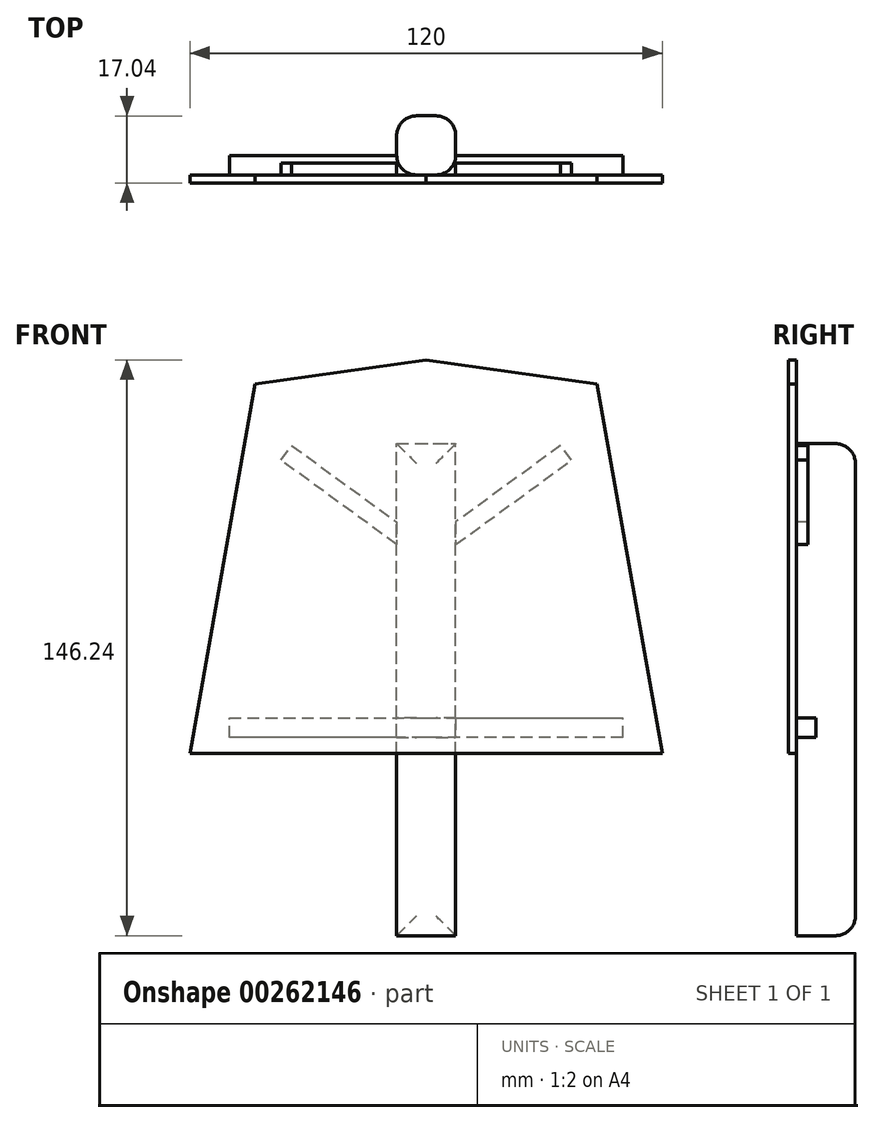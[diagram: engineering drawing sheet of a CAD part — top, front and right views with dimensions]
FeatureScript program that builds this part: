
annotation { "Feature Type Name" : "Feature", "Feature Type Description" : "" }
export const myFeature = defineFeature(function(context is Context, id is Id, definition is map)
    precondition{}
    {
        {
            var Q0;
            Q0=qCreatedBy(makeId("Top.planeOp"),FACE);
            var sketch = newSketch(context, id + "F0", { "sketchPlane" : qUnion([Q0])});
            skLineSegment(sketch, "E0.bottom", {"start": v(-7.5, 15.04) * mm, "end": v(7.5, 15.04) * mm});
            skLineSegment(sketch, "E0.top", {"start": v(-7.5, 0.04) * mm, "end": v(7.5, 0.04) * mm});
            skLineSegment(sketch, "E0.left", {"start": v(-7.5, 15.04) * mm, "end": v(-7.5, 0.04) * mm});
            skLineSegment(sketch, "E0.right", {"start": v(7.5, 15.04) * mm, "end": v(7.5, 0.04) * mm});
            skSolve(sketch);
        }
        {
            var Q0;
            Q0 = qSketchRegion(id + "F0", true);
            extrude(context, id + "F1", {"entities" : qUnion([Q0]), "oppositeDirection" : true, "depth" : 25 * mm});
        }
        {
            var Q0;
            Q0=makeQuery(id+"F1.opExtrude","CAP_FACE",FACE,{"disambiguationData":[OSD([sQuery(id+"F0.wireOp",EDGE,"E0.bottom"),sQuery(id+"F0.wireOp",EDGE,"E0.top"),sQuery(id+"F0.wireOp",EDGE,"E0.left"),sQuery(id+"F0.wireOp",EDGE,"E0.right")])],"isStart":true});
            extrude(context, id + "F2", {"entities" : qUnion([Q0]), "operationType" : NewBodyOperationType.ADD, "depth" : 100 * mm});
        }
        {
            var Q0;
            Q0=qCreatedBy(makeId("Front.planeOp"),FACE);
            var sketch = newSketch(context, id + "F3", { "sketchPlane" : qUnion([Q0])});
            skLineSegment(sketch, "E1", {"start": v(60, 21.24) * mm, "end": v(43.44, 115.13) * mm});
            skLineSegment(sketch, "E2", {"start": v(0, 121.24) * mm, "end": v(43.44, 115.13) * mm});
            skLineSegment(sketch, "E3", {"start": v(0, 21.24) * mm, "end": v(60, 21.24) * mm});
            skLineSegment(sketch, "E4", {"start": v(0, 21.24) * mm, "end": v(0, 121.24) * mm});
            skLineSegment(sketch, "E5.MirrorCS", {"start": v(0, 121.24) * mm, "end": v(-43.44, 115.13) * mm});
            skLineSegment(sketch, "E6.MirrorCS", {"start": v(-60, 21.24) * mm, "end": v(-43.44, 115.13) * mm});
            skLineSegment(sketch, "E7.MirrorCS", {"start": v(0, 21.24) * mm, "end": v(-60, 21.24) * mm});
            skSolve(sketch);
        }
        {
            var Q0;
            Q0=makeQuery(id+"F3.imprint","IMPRINT",FACE,{"disambiguationData":[TD([[makeQuery(id+"F3.imprint","IMPRINT",EDGE,{"derivedFrom":sQuery(id+"F3.wireOp",EDGE,"E4")}),1.0]])]});
            var Q1;
            Q1=makeQuery(id+"F3.imprint","IMPRINT",FACE,{"disambiguationData":[TD([[makeQuery(id+"F3.imprint","IMPRINT",EDGE,{"derivedFrom":sQuery(id+"F3.wireOp",EDGE,"E1")}),1.0]])]});
            extrude(context, id + "F4", {"entities" : qUnion([Q0, Q1]), "operationType" : NewBodyOperationType.ADD, "depth" : 2 * mm});
        }
        {
            var Q0;
            Q0=qCreatedBy(makeId("Front.planeOp"),FACE);
            var sketch = newSketch(context, id + "F5", { "sketchPlane" : qUnion([Q0])});
            skLineSegment(sketch, "E8", {"start": v(0, 25.31) * mm, "end": v(-50, 25.31) * mm});
            skLineSegment(sketch, "E9", {"start": v(-50, 25.31) * mm, "end": v(-50, 30.31) * mm});
            skLineSegment(sketch, "E10", {"start": v(-50, 30.31) * mm, "end": v(0, 30.31) * mm});
            skLineSegment(sketch, "E11", {"start": v(0, 30.31) * mm, "end": v(0, 25.31) * mm});
            skLineSegment(sketch, "E12.MirrorCS", {"start": v(50, 30.31) * mm, "end": v(0, 30.31) * mm});
            skLineSegment(sketch, "E13.MirrorCS", {"start": v(0, 25.31) * mm, "end": v(50, 25.31) * mm});
            skLineSegment(sketch, "E14.MirrorCS", {"start": v(50, 25.31) * mm, "end": v(50, 30.31) * mm});
            skSolve(sketch);
        }
        {
            var Q0;
            Q0=makeQuery(id+"F5.imprint","IMPRINT",FACE,{"disambiguationData":[TD([[makeQuery(id+"F5.imprint","IMPRINT",EDGE,{"derivedFrom":sQuery(id+"F5.wireOp",EDGE,"E8")}),-1.0]])]});
            var Q1;
            Q1=makeQuery(id+"F5.imprint","IMPRINT",FACE,{"disambiguationData":[TD([[makeQuery(id+"F5.imprint","IMPRINT",EDGE,{"derivedFrom":sQuery(id+"F5.wireOp",EDGE,"E11")}),1.0]])]});
            extrude(context, id + "F6", {"entities" : qUnion([Q0, Q1]), "oppositeDirection" : true, "depth" : 5 * mm});
        }
        {
            var Q0;
            Q0=makeQuery(id+"F1.opExtrude","SWEPT_BODY",BODY,{"disambiguationData":[OSD([sQuery(id+"F0.wireOp",EDGE,"E0.bottom"),sQuery(id+"F0.wireOp",EDGE,"E0.top"),sQuery(id+"F0.wireOp",EDGE,"E0.left"),sQuery(id+"F0.wireOp",EDGE,"E0.right")])]});
            var Q1;
            Q1=makeQuery(id+"F6.opExtrude","SWEPT_BODY",BODY,{"disambiguationData":[OSD([sQuery(id+"F5.wireOp",EDGE,"E8"),sQuery(id+"F5.wireOp",EDGE,"E9"),sQuery(id+"F5.wireOp",EDGE,"E10"),sQuery(id+"F5.wireOp",EDGE,"E12.MirrorCS"),sQuery(id+"F5.wireOp",EDGE,"E13.MirrorCS"),sQuery(id+"F5.wireOp",EDGE,"E14.MirrorCS")])]});
            booleanBodies(context, id + "F7", {"operationType" : BooleanOperationType.UNION, "tools" : qUnion([Q0, Q1])});
        }
        {
            var Q0;
            Q0=makeQuery(id+"F4.opExtrude","CAP_FACE",FACE,{"disambiguationData":[OSD([sQuery(id+"F3.wireOp",EDGE,"E1"),sQuery(id+"F3.wireOp",EDGE,"E2"),sQuery(id+"F3.wireOp",EDGE,"E3"),sQuery(id+"F3.wireOp",EDGE,"E5.MirrorCS"),sQuery(id+"F3.wireOp",EDGE,"E6.MirrorCS"),sQuery(id+"F3.wireOp",EDGE,"E7.MirrorCS")])],"isStart":true});
            var sketch = newSketch(context, id + "F8", { "sketchPlane" : qUnion([Q0])});
            skLineSegment(sketch, "E15", {"start": v(7.5, 74.35) * mm, "end": v(36.88, 95.79) * mm});
            skLineSegment(sketch, "E16", {"start": v(36.88, 95.79) * mm, "end": v(34.15, 99.52) * mm});
            skLineSegment(sketch, "E17", {"start": v(34.15, 99.52) * mm, "end": v(7.5, 80.08) * mm});
            skLineSegment(sketch, "E18.MirrorCS", {"start": v(-34.15, 99.52) * mm, "end": v(-7.5, 80.08) * mm});
            skLineSegment(sketch, "E19.MirrorCS", {"start": v(-7.5, 74.35) * mm, "end": v(-36.88, 95.79) * mm});
            skLineSegment(sketch, "E20.MirrorCS", {"start": v(-36.88, 95.79) * mm, "end": v(-34.15, 99.52) * mm});
            skLineSegment(sketch, "E21", {"start": v(-7.5, 80.08) * mm, "end": v(-7.5, 74.35) * mm});
            skLineSegment(sketch, "E22", {"start": v(7.5, 80.08) * mm, "end": v(7.5, 74.35) * mm});
            skSolve(sketch);
        }
        {
            var Q0;
            Q0=makeQuery(id+"F8.imprint","IMPRINT",FACE,{"disambiguationData":[TD([[makeQuery(id+"F8.imprint","IMPRINT",EDGE,{"derivedFrom":sQuery(id+"F8.wireOp",EDGE,"E18.MirrorCS")}),-1.0]])]});
            var Q1;
            Q1=makeQuery(id+"F8.imprint","IMPRINT",FACE,{"disambiguationData":[TD([[makeQuery(id+"F8.imprint","IMPRINT",EDGE,{"derivedFrom":sQuery(id+"F8.wireOp",EDGE,"E15")}),1.0]])]});
            extrude(context, id + "F9", {"entities" : qUnion([Q0, Q1]), "depth" : 3 * mm});
        }
        {
            var Q0;
            {var subQ0=sQuery(id+"F0.wireOp",EDGE,"E0.right");var subQ1=sQuery(id+"F0.wireOp",EDGE,"E0.bottom");Q0=makeQuery(id+"F2.boolean.opBoolean","MERGE",EDGE,{"derivedFrom":[makeQuery(id+"F1.opExtrude","SWEPT_EDGE",EDGE,{"disambiguationData":[OSD([subQ1,subQ0])]}),makeQuery(id+"F2.opExtrude","SWEPT_EDGE",EDGE,{"disambiguationData":[OSD([subQ1,subQ0])]})]});}
            var Q1;
            {var subQ0=sQuery(id+"F0.wireOp",EDGE,"E0.top");var subQ1=sQuery(id+"F0.wireOp",EDGE,"E0.right");Q1=makeQuery(id+"F7.opBoolean","SPLIT",EDGE,{"disambiguationData":[TD([makeQuery(id+"F6.opExtrude","SWEPT_FACE",FACE,{"disambiguationData":[OSD([sQuery(id+"F5.wireOp",EDGE,"E8"),sQuery(id+"F5.wireOp",EDGE,"E13.MirrorCS")])]})])],"derivedFrom":makeQuery(id+"F2.boolean.opBoolean","MERGE",EDGE,{"derivedFrom":[makeQuery(id+"F1.opExtrude","SWEPT_EDGE",EDGE,{"disambiguationData":[OSD([subQ0,subQ1])]}),makeQuery(id+"F2.opExtrude","SWEPT_EDGE",EDGE,{"disambiguationData":[OSD([subQ0,subQ1])]})]})});}
            var Q2;
            {var subQ0=sQuery(id+"F0.wireOp",EDGE,"E0.bottom");Q2=makeQuery(id+"F2.boolean.opBoolean","MERGE",FACE,{"derivedFrom":[makeQuery(id+"F1.opExtrude","SWEPT_FACE",FACE,{"disambiguationData":[OSD([subQ0])]}),makeQuery(id+"F2.opExtrude","SWEPT_FACE",FACE,{"disambiguationData":[OSD([subQ0])]})]});}
            var Q3;
            {var subQ0=sQuery(id+"F0.wireOp",EDGE,"E0.top");var subQ1=sQuery(id+"F0.wireOp",EDGE,"E0.left");Q3=makeQuery(id+"F7.opBoolean","SPLIT",EDGE,{"disambiguationData":[TD([makeQuery(id+"F6.opExtrude","SWEPT_FACE",FACE,{"disambiguationData":[OSD([sQuery(id+"F5.wireOp",EDGE,"E8"),sQuery(id+"F5.wireOp",EDGE,"E13.MirrorCS")])]})])],"derivedFrom":makeQuery(id+"F2.boolean.opBoolean","MERGE",EDGE,{"derivedFrom":[makeQuery(id+"F1.opExtrude","SWEPT_EDGE",EDGE,{"disambiguationData":[OSD([subQ0,subQ1])]}),makeQuery(id+"F2.opExtrude","SWEPT_EDGE",EDGE,{"disambiguationData":[OSD([subQ0,subQ1])]})]})});}
            fillet(context, id + "F10", {"entities" : qUnion([Q0, Q1, Q2, Q3]), "radius" : 5 * mm, "tangentPropagation" : true, "allowEdgeOverflow" : false});
        }
    });
